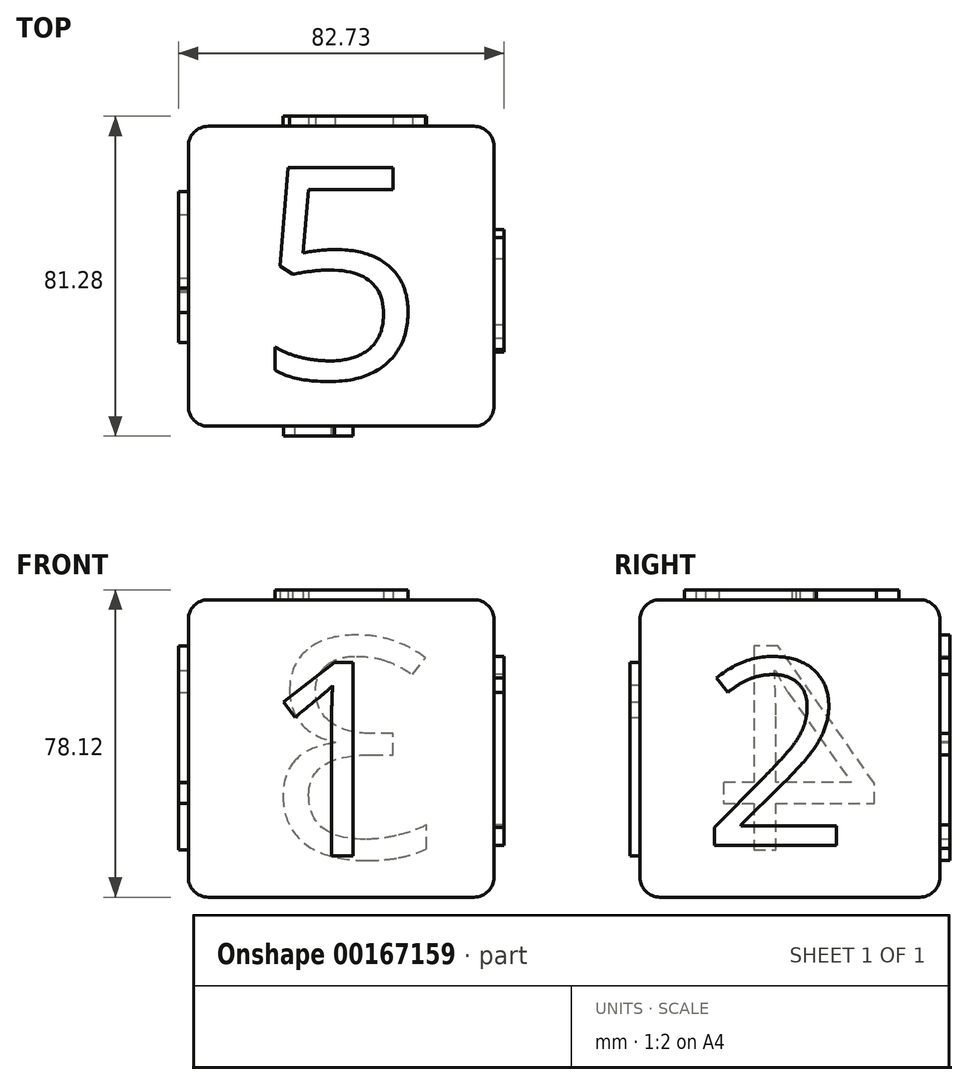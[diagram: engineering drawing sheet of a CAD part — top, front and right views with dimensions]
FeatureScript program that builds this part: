
annotation { "Feature Type Name" : "Feature", "Feature Type Description" : "" }
export const myFeature = defineFeature(function(context is Context, id is Id, definition is map)
    precondition{}
    {
        {
            var Q0;
            Q0=qCreatedBy(makeId("Front.planeOp"),FACE);
            var sketch = newSketch(context, id + "F0", { "sketchPlane" : qUnion([Q0])});
            skLineSegment(sketch, "E0.bottom", {"start": v(-42.96, 33.36) * mm, "end": v(34.7, 33.36) * mm});
            skLineSegment(sketch, "E0.top", {"start": v(-42.96, -42.22) * mm, "end": v(34.7, -42.22) * mm});
            skLineSegment(sketch, "E0.left", {"start": v(-42.96, 33.36) * mm, "end": v(-42.96, -42.22) * mm});
            skLineSegment(sketch, "E0.right", {"start": v(34.7, 33.36) * mm, "end": v(34.7, -42.22) * mm});
            skSolve(sketch);
        }
        {
            var Q0;
            Q0=makeQuery(id+"F0.imprint","IMPRINT",FACE,{"disambiguationData":[TD([[makeQuery(id+"F0.imprint","IMPRINT",EDGE,{"derivedFrom":sQuery(id+"F0.wireOp",EDGE,"E0.bottom")}),-1.0]])]});
            extrude(context, id + "F1", {"entities" : qUnion([Q0]), "depth" : 76.2 * mm});
        }
        {
            var Q0;
            Q0=makeQuery(id+"F1.opExtrude","SWEPT_FACE",FACE,{"disambiguationData":[OSD([sQuery(id+"F0.wireOp",EDGE,"E0.right")])]});
            var Q1;
            Q1=makeQuery(id+"F1.opExtrude","CAP_FACE",FACE,{"disambiguationData":[OSD([sQuery(id+"F0.wireOp",EDGE,"E0.bottom"),sQuery(id+"F0.wireOp",EDGE,"E0.top"),sQuery(id+"F0.wireOp",EDGE,"E0.left"),sQuery(id+"F0.wireOp",EDGE,"E0.right")])],"isStart":false});
            var Q2;
            Q2=makeQuery(id+"F1.opExtrude","SWEPT_FACE",FACE,{"disambiguationData":[OSD([sQuery(id+"F0.wireOp",EDGE,"E0.bottom")])]});
            var Q3;
            Q3=makeQuery(id+"F1.opExtrude","CAP_FACE",FACE,{"disambiguationData":[OSD([sQuery(id+"F0.wireOp",EDGE,"E0.bottom"),sQuery(id+"F0.wireOp",EDGE,"E0.top"),sQuery(id+"F0.wireOp",EDGE,"E0.left"),sQuery(id+"F0.wireOp",EDGE,"E0.right")])],"isStart":true});
            var Q4;
            Q4=makeQuery(id+"F1.opExtrude","SWEPT_FACE",FACE,{"disambiguationData":[OSD([sQuery(id+"F0.wireOp",EDGE,"E0.top")])]});
            fillet(context, id + "F2", {"entities" : qUnion([Q0, Q1, Q2, Q3, Q4]), "radius" : 5.08 * mm, "tangentPropagation" : true, "allowEdgeOverflow" : false});
        }
        {
            var Q0;
            Q0=makeQuery(id+"F1.opExtrude","SWEPT_FACE",FACE,{"disambiguationData":[OSD([sQuery(id+"F0.wireOp",EDGE,"E0.right")])]});
            var sketch = newSketch(context, id + "F3", { "sketchPlane" : qUnion([Q0])});
            skText(sketch, "E1", { "text": "2", "fontName": "OpenSans-Regular.ttf"});
            const initialGuessF3  = {"E1": [-0.06056, -0.02907, 1, 0, 0.04773]};
            skSetInitialGuess(sketch, initialGuessF3);
            skSolve(sketch);
        }
        {
            var Q0;
            Q0 = qSketchRegion(id + "F3", true);
            extrude(context, id + "F4", {"entities" : qUnion([Q0]), "operationType" : NewBodyOperationType.ADD, "depth" : 2.54 * mm});
        }
        {
            var Q0;
            Q0=makeQuery(id+"F1.opExtrude","CAP_FACE",FACE,{"disambiguationData":[OSD([sQuery(id+"F0.wireOp",EDGE,"E0.bottom"),sQuery(id+"F0.wireOp",EDGE,"E0.top"),sQuery(id+"F0.wireOp",EDGE,"E0.left"),sQuery(id+"F0.wireOp",EDGE,"E0.right")])],"isStart":true});
            var sketch = newSketch(context, id + "F5", { "sketchPlane" : qUnion([Q0])});
            skText(sketch, "E2", { "text": "3", "fontName": "OpenSans-Regular.ttf"});
            const initialGuessF5  = {"E2": [-0.02114, -0.03212, 1, 0, 0.05621]};
            skSetInitialGuess(sketch, initialGuessF5);
            skSolve(sketch);
        }
        {
            var Q0;
            Q0 = qSketchRegion(id + "F5", true);
            extrude(context, id + "F6", {"entities" : qUnion([Q0]), "operationType" : NewBodyOperationType.ADD, "depth" : 2.54 * mm});
        }
        {
            var Q0;
            Q0=makeQuery(id+"F1.opExtrude","SWEPT_FACE",FACE,{"disambiguationData":[OSD([sQuery(id+"F0.wireOp",EDGE,"E0.left")])]});
            var sketch = newSketch(context, id + "F7", { "sketchPlane" : qUnion([Q0])});
            skText(sketch, "E3", { "text": "4", "fontName": "OpenSans-Regular.ttf"});
            const initialGuessF7  = {"E3": [0.01512, -0.03025, 1, 0, 0.05196]};
            skSetInitialGuess(sketch, initialGuessF7);
            skSolve(sketch);
        }
        {
            var Q0;
            Q0 = qSketchRegion(id + "F7", true);
            extrude(context, id + "F8", {"entities" : qUnion([Q0]), "operationType" : NewBodyOperationType.ADD, "depth" : 2.54 * mm});
        }
        {
            var Q0;
            Q0=makeQuery(id+"F1.opExtrude","CAP_FACE",FACE,{"disambiguationData":[OSD([sQuery(id+"F0.wireOp",EDGE,"E0.bottom"),sQuery(id+"F0.wireOp",EDGE,"E0.top"),sQuery(id+"F0.wireOp",EDGE,"E0.left"),sQuery(id+"F0.wireOp",EDGE,"E0.right")])],"isStart":false});
            var sketch = newSketch(context, id + "F9", { "sketchPlane" : qUnion([Q0])});
            skText(sketch, "E4", { "text": "1", "fontName": "OpenSans-Regular.ttf"});
            const initialGuessF9  = {"E4": [-0.02513, -0.03171, 1, 0, 0.04952]};
            skSetInitialGuess(sketch, initialGuessF9);
            skSolve(sketch);
        }
        {
            var Q0;
            Q0 = qSketchRegion(id + "F9", true);
            extrude(context, id + "F10", {"entities" : qUnion([Q0]), "operationType" : NewBodyOperationType.ADD, "depth" : 2.54 * mm});
        }
        {
            var Q0;
            Q0=makeQuery(id+"F1.opExtrude","SWEPT_FACE",FACE,{"disambiguationData":[OSD([sQuery(id+"F0.wireOp",EDGE,"E0.bottom")])]});
            var sketch = newSketch(context, id + "F11", { "sketchPlane" : qUnion([Q0])});
            skText(sketch, "E5", { "text": "5", "fontName": "OpenSans-Regular.ttf"});
            const initialGuessF11  = {"E5": [-0.0258, -0.06411, 1, 0, 0.05413]};
            skSetInitialGuess(sketch, initialGuessF11);
            skSolve(sketch);
        }
        {
            var Q0;
            Q0 = qSketchRegion(id + "F11", true);
            extrude(context, id + "F12", {"entities" : qUnion([Q0]), "operationType" : NewBodyOperationType.ADD, "depth" : 2.54 * mm});
        }
    });
